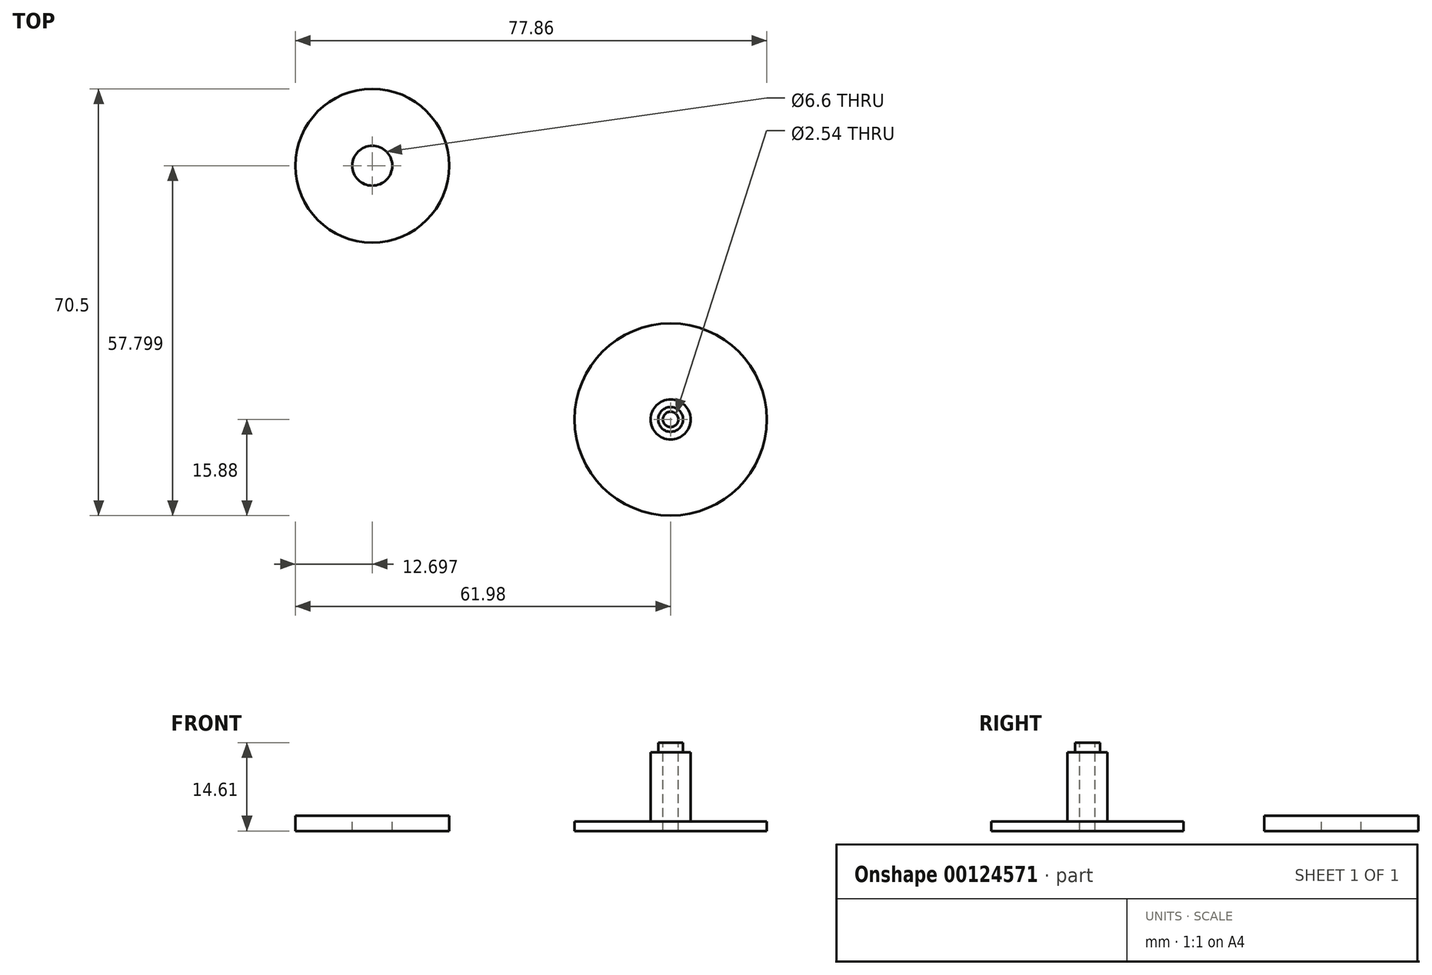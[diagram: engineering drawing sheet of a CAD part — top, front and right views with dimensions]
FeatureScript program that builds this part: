
annotation { "Feature Type Name" : "Feature", "Feature Type Description" : "" }
export const myFeature = defineFeature(function(context is Context, id is Id, definition is map)
    precondition{}
    {
        {
            var Q0;
            Q0=qCreatedBy(makeId("Top.planeOp"),FACE);
            var sketch = newSketch(context, id + "F0", { "sketchPlane" : qUnion([Q0])});
            skCircle(sketch, "E0", {"center": v(0, 0) * mm, "radius": 15.88 * mm});
            skSolve(sketch);
        }
        {
            var Q0;
            Q0=makeQuery(id+"F0.imprint","IMPRINT",FACE,{"disambiguationData":[TD([[makeQuery(id+"F0.imprint","IMPRINT",EDGE,{"derivedFrom":sQuery(id+"F0.wireOp",EDGE,"E0")}),1.0]])]});
            var sketch = newSketch(context, id + "F1", { "sketchPlane" : qUnion([Q0])});
            skSolve(sketch);
        }
        {
            var Q0;
            Q0=makeQuery(id+"F0.imprint","IMPRINT",FACE,{"disambiguationData":[TD([[makeQuery(id+"F0.imprint","IMPRINT",EDGE,{"derivedFrom":sQuery(id+"F0.wireOp",EDGE,"E0")}),1.0]])]});
            extrude(context, id + "F2", {"entities" : qUnion([Q0]), "depth" : 1.59 * mm});
        }
        {
            var Q0;
            Q0=makeQuery(id+"F2.opExtrude","CAP_FACE",FACE,{"disambiguationData":[OSD([sQuery(id+"F0.wireOp",EDGE,"E0")])],"isStart":false});
            var sketch = newSketch(context, id + "F3", { "sketchPlane" : qUnion([Q0])});
            skCircle(sketch, "E1", {"center": v(0, 0) * mm, "radius": 3.3 * mm});
            skSolve(sketch);
        }
        {
            var Q0;
            Q0 = qSketchRegion(id + "F3", true);
            extrude(context, id + "F4", {"entities" : qUnion([Q0]), "operationType" : NewBodyOperationType.ADD, "depth" : 11.43 * mm});
        }
        {
            var Q0;
            Q0=makeQuery(id+"F4.opExtrude","CAP_FACE",FACE,{"disambiguationData":[OSD([sQuery(id+"F3.wireOp",EDGE,"E1")])],"isStart":false});
            var sketch = newSketch(context, id + "F5", { "sketchPlane" : qUnion([Q0])});
            skCircle(sketch, "E2", {"center": v(0, 0) * mm, "radius": 2.04 * mm});
            skSolve(sketch);
        }
        {
            var Q0;
            Q0 = qSketchRegion(id + "F5", true);
            extrude(context, id + "F6", {"entities" : qUnion([Q0]), "operationType" : NewBodyOperationType.ADD, "depth" : 1.59 * mm});
        }
        {
            var Q0;
            Q0=makeQuery(id+"F6.opExtrude","CAP_FACE",FACE,{"disambiguationData":[OSD([sQuery(id+"F5.wireOp",EDGE,"E2")])],"isStart":false});
            var sketch = newSketch(context, id + "F7", { "sketchPlane" : qUnion([Q0])});
            skCircle(sketch, "E3", {"center": v(0, 0) * mm, "radius": 1.27 * mm});
            skSolve(sketch);
        }
        {
            var Q0;
            Q0 = qSketchRegion(id + "F7", true);
            extrude(context, id + "F8", {"entities" : qUnion([Q0]), "operationType" : NewBodyOperationType.REMOVE, "oppositeDirection" : true, "depth" : 19.05 * mm});
        }
        {
            var Q0;
            Q0=makeQuery(id+"F1.imprint","IMPRINT",FACE,{"disambiguationData":[TD([[makeQuery(id+"F1.imprint","IMPRINT",EDGE,{"derivedFrom":makeQuery(id+"F0.imprint","IMPRINT",EDGE,{"derivedFrom":sQuery(id+"F0.wireOp",EDGE,"E0")})}),1.0]])]});
            var sketch = newSketch(context, id + "F9", { "sketchPlane" : qUnion([Q0])});
            skCircle(sketch, "E4", {"center": v(0, 0) * mm, "radius": 2.67 * mm});
            skSolve(sketch);
        }
        {
            var Q0;
            Q0 = qSketchRegion(id + "F9", true);
            extrude(context, id + "F10", {"entities" : qUnion([Q0]), "operationType" : NewBodyOperationType.REMOVE, "oppositeDirection" : true, "depth" : 6.35 * mm});
        }
        {
            var Q0;
            Q0=qCreatedBy(makeId("Top.planeOp"),FACE);
            var sketch = newSketch(context, id + "F11", { "sketchPlane" : qUnion([Q0])});
            skCircle(sketch, "E5", {"center": v(-49.28, 41.92) * mm, "radius": 12.7 * mm});
            skSolve(sketch);
        }
        {
            var Q0;
            Q0 = qSketchRegion(id + "F11", true);
            extrude(context, id + "F12", {"entities" : qUnion([Q0]), "depth" : 2.54 * mm});
        }
        {
            var Q0;
            Q0=makeQuery(id+"F12.opExtrude","CAP_FACE",FACE,{"disambiguationData":[OSD([sQuery(id+"F11.wireOp",EDGE,"E5")])],"isStart":false});
            var sketch = newSketch(context, id + "F13", { "sketchPlane" : qUnion([Q0])});
            skCircle(sketch, "E6", {"center": v(-49.28, 41.92) * mm, "radius": 3.3 * mm});
            skSolve(sketch);
        }
        {
            var Q0;
            Q0 = qSketchRegion(id + "F13", true);
            extrude(context, id + "F14", {"entities" : qUnion([Q0]), "operationType" : NewBodyOperationType.REMOVE, "oppositeDirection" : true, "depth" : 2.54 * mm});
        }
    });
